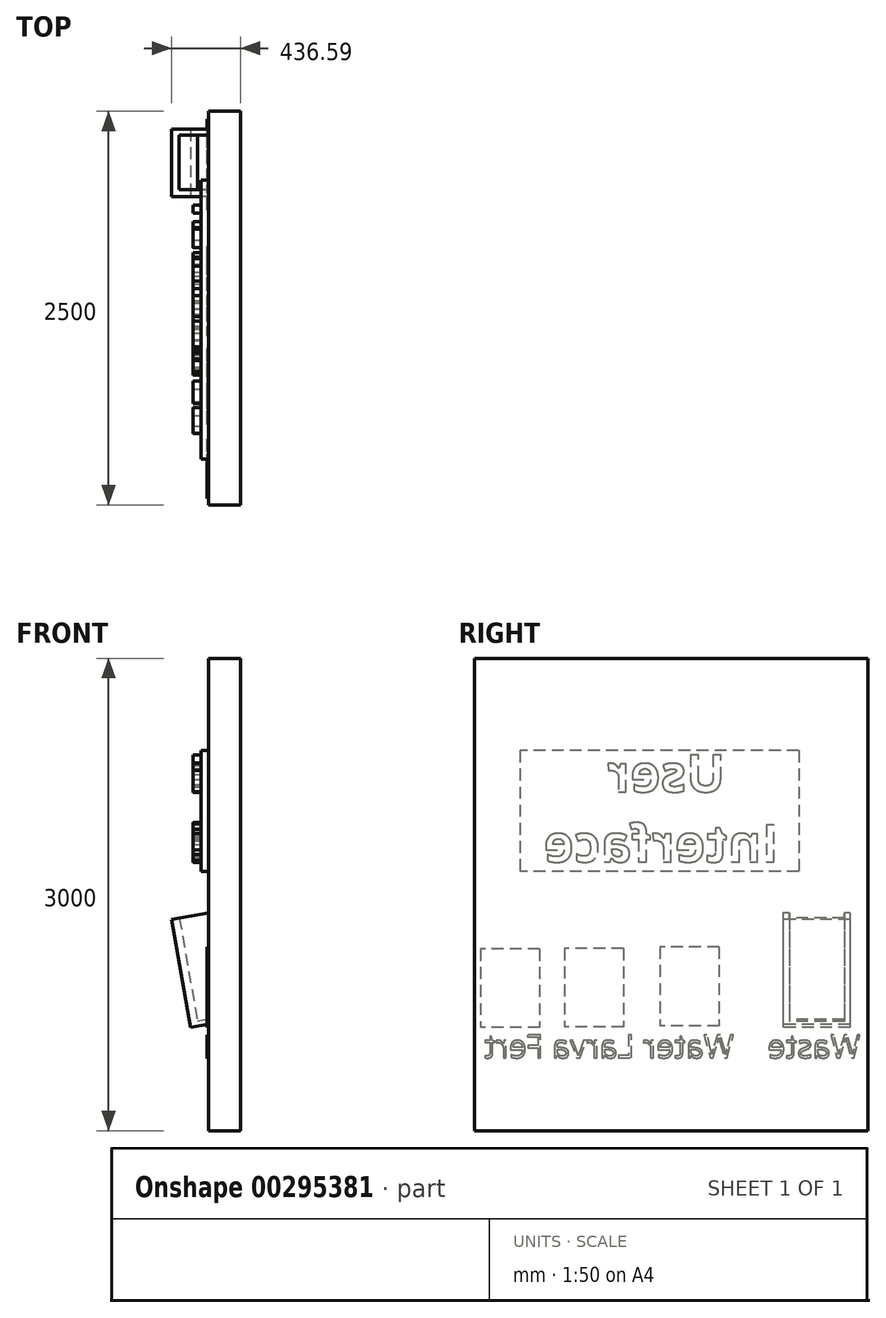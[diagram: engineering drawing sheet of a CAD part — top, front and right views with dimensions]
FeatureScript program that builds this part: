
annotation { "Feature Type Name" : "Feature", "Feature Type Description" : "" }
export const myFeature = defineFeature(function(context is Context, id is Id, definition is map)
    precondition{}
    {
        {
            var Q0;
            Q0=qCreatedBy(makeId("Right.planeOp"),FACE);
            var sketch = newSketch(context, id + "F0", { "sketchPlane" : qUnion([Q0])});
            skLineSegment(sketch, "E0.bottom", {"start": v(0, 0) * mm, "end": v(2500, 0) * mm});
            skLineSegment(sketch, "E0.top", {"start": v(0, 3000) * mm, "end": v(2500, 3000) * mm});
            skLineSegment(sketch, "E0.left", {"start": v(0, 0) * mm, "end": v(0, 3000) * mm});
            skLineSegment(sketch, "E0.right", {"start": v(2500, 0) * mm, "end": v(2500, 3000) * mm});
            skSolve(sketch);
        }
        {
            var Q0;
            Q0 = qSketchRegion(id + "F0", true);
            extrude(context, id + "F1", {"entities" : qUnion([Q0]), "oppositeDirection" : true, "depth" : 200 * mm});
        }
        {
            var Q0;
            Q0=makeQuery(id+"F1.opExtrude","CAP_FACE",FACE,{"disambiguationData":[OSD([sQuery(id+"F0.wireOp",EDGE,"E0.bottom"),sQuery(id+"F0.wireOp",EDGE,"E0.top"),sQuery(id+"F0.wireOp",EDGE,"E0.left"),sQuery(id+"F0.wireOp",EDGE,"E0.right")])],"isStart":false});
            var Q1;
            Q1=makeQuery(id+"F1.opExtrude","CAP_EDGE",EDGE,{"disambiguationData":[OSD([sQuery(id+"F0.wireOp",EDGE,"E0.bottom")])],"isStart":false});
            cPlane(context, id + "F2", {"entities" : qUnion([Q0, Q1]), "cplaneType" : CPlaneType.LINE_ANGLE, "offset" : 25 * mm, "angle" : 10 * degree, "oppositeDirection" : true, "width" : 150 * mm, "height" : 150 * mm});
        }
        {
            var Q0;
            Q0=qCreatedBy(id+"F2.planeOp",FACE);
            var sketch = newSketch(context, id + "F3", { "sketchPlane" : qUnion([Q0])});
            skLineSegment(sketch, "E1.bottom", {"start": v(2386.12, 1397.22) * mm, "end": v(1959.2, 1397.22) * mm});
            skLineSegment(sketch, "E1.top", {"start": v(2386.12, 700.52) * mm, "end": v(1959.2, 700.52) * mm});
            skLineSegment(sketch, "E1.left", {"start": v(2386.12, 1397.22) * mm, "end": v(2386.12, 700.52) * mm});
            skLineSegment(sketch, "E1.right", {"start": v(1959.2, 1397.22) * mm, "end": v(1959.2, 700.52) * mm});
            skSolve(sketch);
        }
        {
            var Q0;
            Q0 = qSketchRegion(id + "F3", true);
            extrude(context, id + "F4", {"entities" : qUnion([Q0]), "operationType" : NewBodyOperationType.ADD, "endBound" : BoundingType.UP_TO_NEXT, "depth" : 25 * mm});
        }
        {
            var Q0;
            Q0=qCreatedBy(id+"F2.planeOp",FACE);
            cPlane(context, id + "F5", {"entities" : qUnion([Q0]), "cplaneType" : CPlaneType.OFFSET, "offset" : 50 * mm, "width" : 150 * mm, "height" : 150 * mm});
        }
        {
            var Q0;
            Q0=qCreatedBy(id+"F5.planeOp",FACE);
            var sketch = newSketch(context, id + "F6", { "sketchPlane" : qUnion([Q0])});
            skLineSegment(sketch, "E2.bottom", {"start": v(2349.67, 1482.87) * mm, "end": v(2000.93, 1482.87) * mm});
            skLineSegment(sketch, "E2.top", {"start": v(2349.67, 730.76) * mm, "end": v(2000.93, 730.76) * mm});
            skLineSegment(sketch, "E2.left", {"start": v(2349.67, 1482.87) * mm, "end": v(2349.67, 730.76) * mm});
            skLineSegment(sketch, "E2.right", {"start": v(2000.93, 1482.87) * mm, "end": v(2000.93, 730.76) * mm});
            skSolve(sketch);
        }
        {
            var Q0;
            Q0 = qSketchRegion(id + "F6", true);
            var Q1;
            Q1=makeQuery(id+"F1.opExtrude","CAP_FACE",FACE,{"disambiguationData":[OSD([sQuery(id+"F0.wireOp",EDGE,"E0.bottom"),sQuery(id+"F0.wireOp",EDGE,"E0.top"),sQuery(id+"F0.wireOp",EDGE,"E0.left"),sQuery(id+"F0.wireOp",EDGE,"E0.right")])],"isStart":false});
            extrude(context, id + "F7", {"entities" : qUnion([Q0]), "operationType" : NewBodyOperationType.REMOVE, "endBound" : BoundingType.UP_TO_SURFACE, "endBoundEntityFace" : qUnion([Q1]), "depth" : 25 * mm});
        }
        {
            var Q0;
            {var subQ0=sQuery(id+"F0.wireOp",EDGE,"E0.right");var subQ1=sQuery(id+"F0.wireOp",EDGE,"E0.left");var subQ2=sQuery(id+"F0.wireOp",EDGE,"E0.top");var subQ3=sQuery(id+"F0.wireOp",EDGE,"E0.bottom");Q0=makeQuery(id+"F7.boolean.opBoolean","MERGE",FACE,{"derivedFrom":[makeQuery(id+"F1.opExtrude","CAP_FACE",FACE,{"disambiguationData":[OSD([subQ3,subQ2,subQ1,subQ0])],"isStart":false}),makeQuery(id+"F7.opExtrude","CAP_FACE",FACE,{"disambiguationData":[OSD([subQ3,subQ2,subQ1,subQ0])],"isStart":false})]});}
            var sketch = newSketch(context, id + "F8", { "sketchPlane" : qUnion([Q0])});
            skLineSegment(sketch, "E3.bottom", {"start": v(-2061.31, 2414.44) * mm, "end": v(-290.44, 2414.44) * mm});
            skLineSegment(sketch, "E3.top", {"start": v(-2061.31, 1646.86) * mm, "end": v(-290.44, 1646.86) * mm});
            skLineSegment(sketch, "E3.left", {"start": v(-2061.31, 2414.44) * mm, "end": v(-2061.31, 1646.86) * mm});
            skLineSegment(sketch, "E3.right", {"start": v(-290.44, 2414.44) * mm, "end": v(-290.44, 1646.86) * mm});
            skSolve(sketch);
        }
        {
            var Q0;
            Q0 = qSketchRegion(id + "F8", true);
            extrude(context, id + "F9", {"entities" : qUnion([Q0]), "operationType" : NewBodyOperationType.ADD, "depth" : 50 * mm});
        }
        {
            var Q0;
            Q0=makeQuery(id+"F9.opExtrude","CAP_FACE",FACE,{"disambiguationData":[OSD([sQuery(id+"F8.wireOp",EDGE,"E3.bottom"),sQuery(id+"F8.wireOp",EDGE,"E3.top"),sQuery(id+"F8.wireOp",EDGE,"E3.left"),sQuery(id+"F8.wireOp",EDGE,"E3.right")])],"isStart":false});
            var sketch = newSketch(context, id + "F10", { "sketchPlane" : qUnion([Q0])});
            skText(sketch, "E4", { "text": "    User \nInterface", "fontName": "OpenSans-Bold.ttf"});
            const initialGuessF10  = {"E4": [-1.93223, 2.1521, 1, 0, 0.23553]};
            skSetInitialGuess(sketch, initialGuessF10);
            skSolve(sketch);
        }
        {
            var Q0;
            Q0 = qSketchRegion(id + "F10", true);
            var Q1;
            Q1 = qConstructionFilter(qBodyType(qCreatedBy(id + "F10" ,EDGE), BodyType.WIRE), ConstructionObject.NO);
            extrude(context, id + "F11", {"entities" : qUnion([Q0]), "operationType" : NewBodyOperationType.ADD, "surfaceEntities" : qUnion([Q1]), "depth" : 50 * mm});
        }
        {
            var Q0;
            {var subQ0=sQuery(id+"F0.wireOp",EDGE,"E0.right");var subQ1=sQuery(id+"F0.wireOp",EDGE,"E0.left");var subQ2=sQuery(id+"F0.wireOp",EDGE,"E0.top");var subQ3=sQuery(id+"F0.wireOp",EDGE,"E0.bottom");Q0=makeQuery(id+"F7.boolean.opBoolean","MERGE",FACE,{"derivedFrom":[makeQuery(id+"F1.opExtrude","CAP_FACE",FACE,{"disambiguationData":[OSD([subQ3,subQ2,subQ1,subQ0])],"isStart":false}),makeQuery(id+"F7.opExtrude","CAP_FACE",FACE,{"disambiguationData":[OSD([subQ3,subQ2,subQ1,subQ0])],"isStart":false})]});}
            var sketch = newSketch(context, id + "F12", { "sketchPlane" : qUnion([Q0])});
            skLineSegment(sketch, "E5.bottom", {"start": v(-1553.95, 1166.36) * mm, "end": v(-1178.95, 1166.36) * mm});
            skLineSegment(sketch, "E5.top", {"start": v(-1553.95, 666.36) * mm, "end": v(-1178.95, 666.36) * mm});
            skLineSegment(sketch, "E5.left", {"start": v(-1553.95, 1166.36) * mm, "end": v(-1553.95, 666.36) * mm});
            skLineSegment(sketch, "E5.right", {"start": v(-1178.95, 1166.36) * mm, "end": v(-1178.95, 666.36) * mm});
            skText(sketch, "E6", { "text": "Waste    Water Larva Fert", "fontName": "OpenSans-Regular.ttf"});
            skLineSegment(sketch, "E7.bottom", {"start": v(-945.93, 1158) * mm, "end": v(-570.93, 1158) * mm});
            skLineSegment(sketch, "E7.top", {"start": v(-945.93, 658) * mm, "end": v(-570.93, 658) * mm});
            skLineSegment(sketch, "E7.left", {"start": v(-945.93, 1158) * mm, "end": v(-945.93, 658) * mm});
            skLineSegment(sketch, "E7.right", {"start": v(-570.93, 1158) * mm, "end": v(-570.93, 658) * mm});
            skLineSegment(sketch, "E8.bottom", {"start": v(-414.75, 1154.44) * mm, "end": v(-39.75, 1154.44) * mm});
            skLineSegment(sketch, "E8.top", {"start": v(-414.75, 654.44) * mm, "end": v(-39.75, 654.44) * mm});
            skLineSegment(sketch, "E8.left", {"start": v(-414.75, 1154.44) * mm, "end": v(-414.75, 654.44) * mm});
            skLineSegment(sketch, "E8.right", {"start": v(-39.75, 1154.44) * mm, "end": v(-39.75, 654.44) * mm});
            const initialGuessF12  = {"E6": [-2.45216, 0.46246, 1, 0, 0.14821]};
            skSetInitialGuess(sketch, initialGuessF12);
            skSolve(sketch);
        }
        {
            var Q0;
            Q0 = qSketchRegion(id + "F12", true);
            extrude(context, id + "F13", {"entities" : qUnion([Q0]), "operationType" : NewBodyOperationType.ADD, "depth" : 10 * mm});
        }
    });
